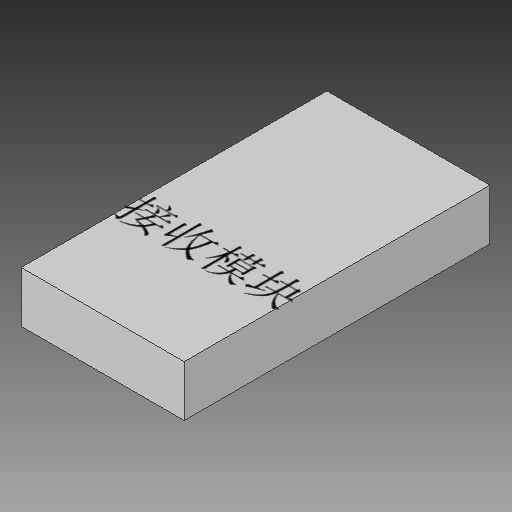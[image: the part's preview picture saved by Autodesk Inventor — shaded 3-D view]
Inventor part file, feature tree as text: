
AUTODESK INVENTOR PART (.ipt)
format: ipt  version: 2018 (Build 220112000, 112)  size: 90,624 bytes
history: native  units: mm
features: sketch x2, extrude x1
ambient origin geometry x8: Origin, YZ Plane, XZ Plane, XY Plane, X Axis, Y Axis, Z Axis, Center Point
bodies: 实体1 (feature_tree)
feature tree (3):
  extrude  "拉伸1"  Depth=16.0mm
  sketch  "草图2"  dims[d2=5.0mm d3=0.0mm]
  sketch  "草图1"  dims[d0=30.0mm d1=16.0mm]
